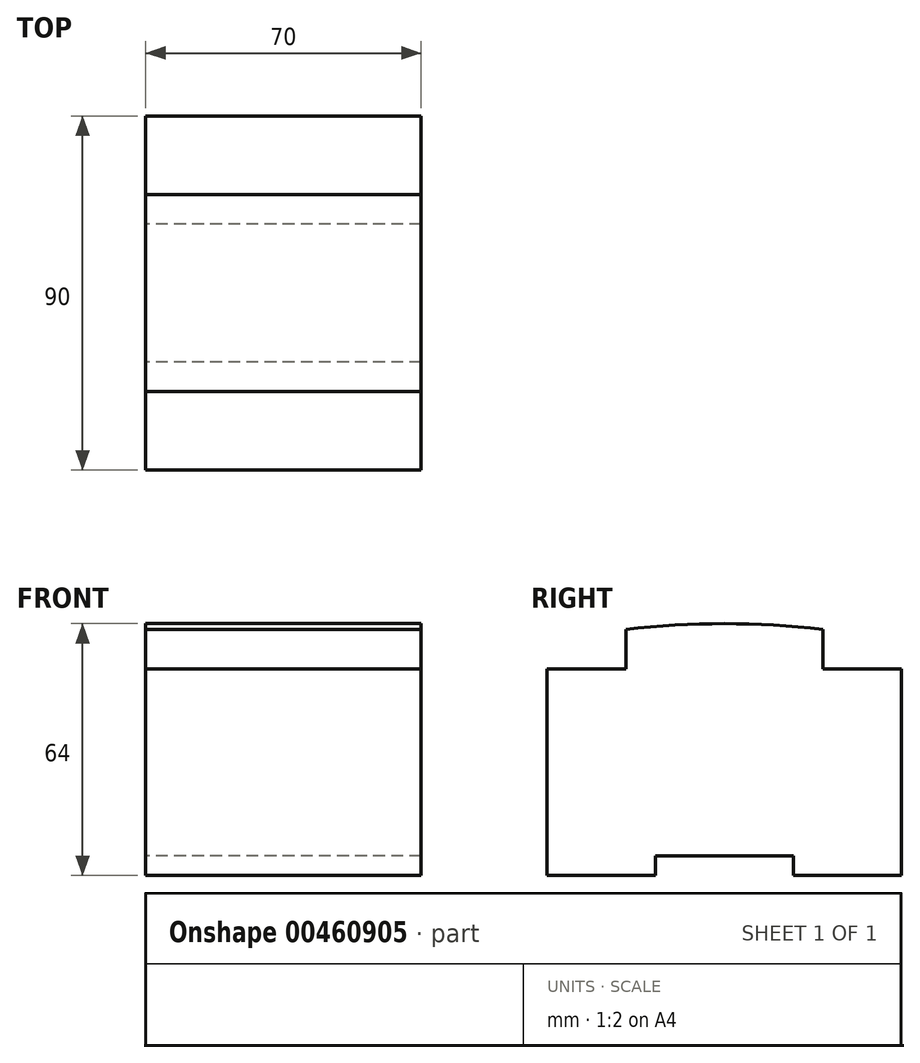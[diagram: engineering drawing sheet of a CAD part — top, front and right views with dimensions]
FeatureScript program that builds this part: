
annotation { "Feature Type Name" : "Feature", "Feature Type Description" : "" }
export const myFeature = defineFeature(function(context is Context, id is Id, definition is map)
    precondition{}
    {
        {
            var Q0;
            Q0=qCreatedBy(makeId("Right.planeOp"),FACE);
            var sketch = newSketch(context, id + "F0", { "sketchPlane" : qUnion([Q0])});
            skLineSegment(sketch, "E0", {"start": v(-17.5, 0) * mm, "end": v(-17.5, -5) * mm});
            skLineSegment(sketch, "E1", {"start": v(-17.5, -5) * mm, "end": v(-45, -5) * mm});
            skLineSegment(sketch, "E2", {"start": v(-45, -5) * mm, "end": v(-45, 47.5) * mm});
            skLineSegment(sketch, "E3", {"start": v(-45, 47.5) * mm, "end": v(-25, 47.5) * mm});
            skLineSegment(sketch, "E4", {"start": v(-25, 47.5) * mm, "end": v(-25, 57.5) * mm});
            skLineSegment(sketch, "E5", {"start": v(-17.5, 0) * mm, "end": v(0, 0) * mm});
            skArc(sketch, "E6", {"start": v(0, 59) * mm, "mid": v(-12.52, 58.62) * mm, "end": v(-25, 57.5) * mm});
            skLineSegment(sketch, "E7", {"start": v(0, 59) * mm, "end": v(43.97, 59) * mm, "construction": true});
            skLineSegment(sketch, "E8", {"start": v(0, 59) * mm, "end": v(0, 0) * mm, "construction": true});
            skArc(sketch, "E9.MirrorCS", {"start": v(0, 59) * mm, "mid": v(12.52, 58.62) * mm, "end": v(25, 57.5) * mm});
            skLineSegment(sketch, "E10.MirrorCS", {"start": v(17.5, -5) * mm, "end": v(45, -5) * mm});
            skLineSegment(sketch, "E11.MirrorCS", {"start": v(45, -5) * mm, "end": v(45, 47.5) * mm});
            skLineSegment(sketch, "E12.MirrorCS", {"start": v(25, 47.5) * mm, "end": v(25, 57.5) * mm});
            skLineSegment(sketch, "E13.MirrorCS", {"start": v(17.5, 0) * mm, "end": v(17.5, -5) * mm});
            skLineSegment(sketch, "E14.MirrorCS", {"start": v(17.5, 0) * mm, "end": v(0, 0) * mm});
            skLineSegment(sketch, "E15.MirrorCS", {"start": v(45, 47.5) * mm, "end": v(25, 47.5) * mm});
            skSolve(sketch);
        }
        {
            var Q0;
            Q0=makeQuery(id+"F0.imprint","IMPRINT",FACE,{"disambiguationData":[TD([[makeQuery(id+"F0.imprint","IMPRINT",EDGE,{"derivedFrom":sQuery(id+"F0.wireOp",EDGE,"E0")}),-1.0]])]});
            extrude(context, id + "F1", {"entities" : qUnion([Q0]), "depth" : 70 * mm, "offsetDistance" : 25 * mm, "symmetric" : true});
        }
    });
